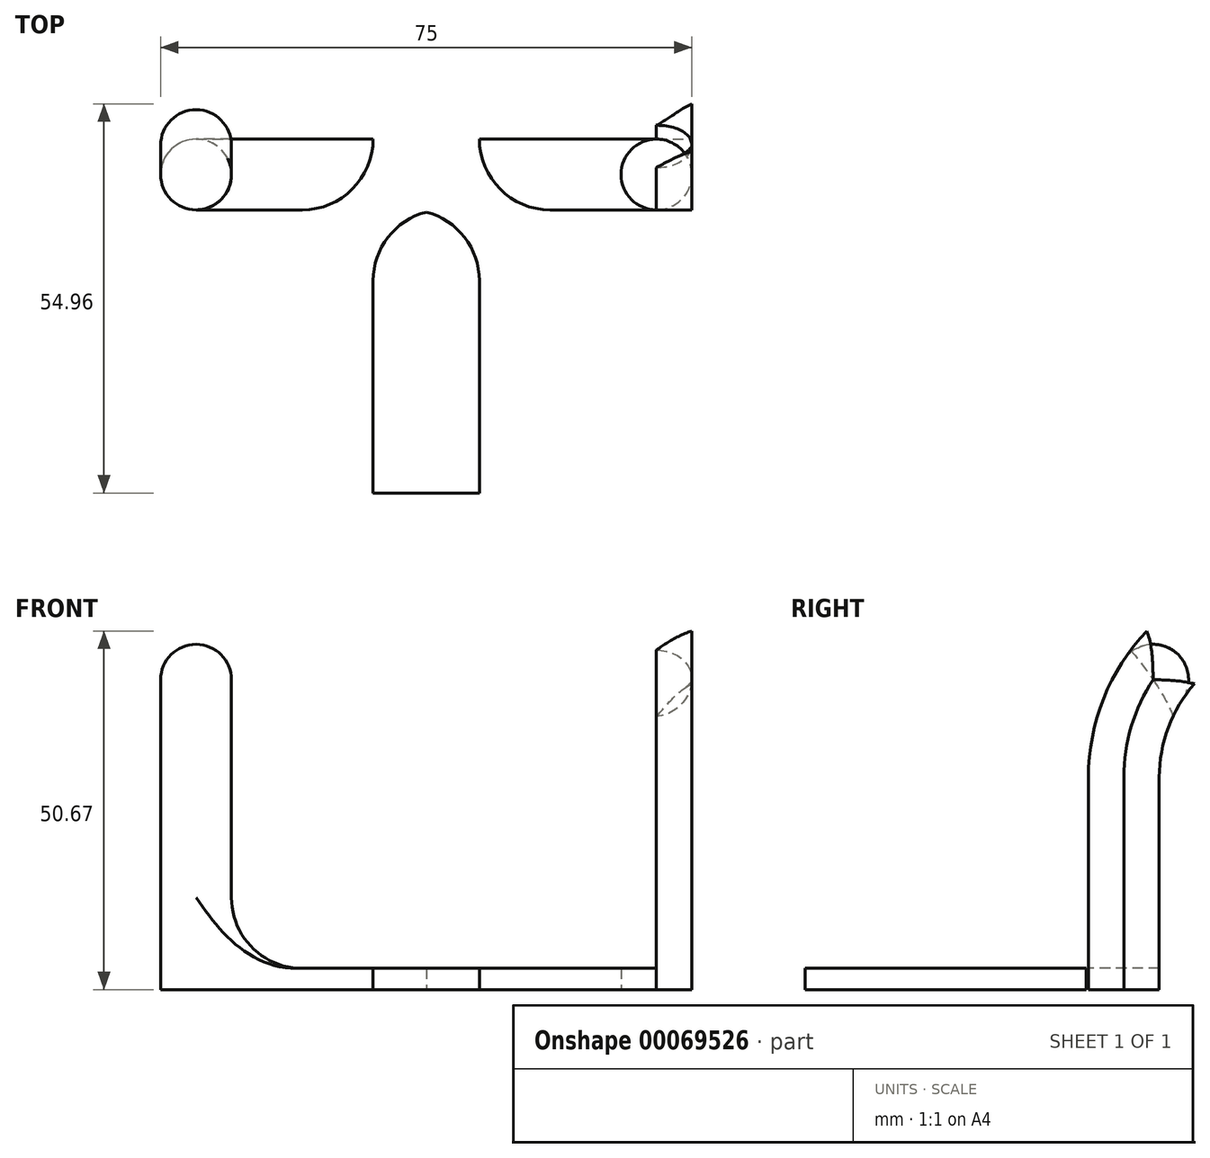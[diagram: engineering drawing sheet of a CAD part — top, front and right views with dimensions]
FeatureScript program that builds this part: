
annotation { "Feature Type Name" : "Feature", "Feature Type Description" : "" }
export const myFeature = defineFeature(function(context is Context, id is Id, definition is map)
    precondition{}
    {
        {
            var Q0;
            Q0=qCreatedBy(makeId("Top.planeOp"),FACE);
            var sketch = newSketch(context, id + "F0", { "sketchPlane" : qUnion([Q0])});
            skLineSegment(sketch, "E0.bottom", {"start": v(-37.5, -5) * mm, "end": v(37.5, -5) * mm});
            skLineSegment(sketch, "E0.top", {"start": v(-37.5, 5) * mm, "end": v(37.5, 5) * mm});
            skLineSegment(sketch, "E0.left", {"start": v(-37.5, -5) * mm, "end": v(-37.5, 5) * mm});
            skLineSegment(sketch, "E0.right", {"start": v(37.5, -5) * mm, "end": v(37.5, 5) * mm});
            skPoint(sketch, "E0.middle", {"position": v(0, 0) * mm});
            skLineSegment(sketch, "E1", {"start": v(0, 0) * mm, "end": v(0, 5) * mm, "construction": true});
            skCircle(sketch, "E2", {"center": v(-32.5, 0) * mm, "radius": 5 * mm});
            skCircle(sketch, "E3.MirrorC", {"center": v(32.5, 0) * mm, "radius": 5 * mm});
            skLineSegment(sketch, "E4.bottom", {"start": v(7.5, -45) * mm, "end": v(-7.5, -45) * mm});
            skLineSegment(sketch, "E4.top", {"start": v(7.5, 5) * mm, "end": v(-7.5, 5) * mm});
            skLineSegment(sketch, "E4.left", {"start": v(7.5, -45) * mm, "end": v(7.5, 5) * mm});
            skLineSegment(sketch, "E4.right", {"start": v(-7.5, -45) * mm, "end": v(-7.5, 5) * mm});
            skPoint(sketch, "E4.middle", {"position": v(0, -20) * mm});
            skSolve(sketch);
        }
        {
            var Q0;
            {var subQ0=sQuery(id+"F0.wireOp",EDGE,"E3.MirrorC");var subQ1=makeQuery(id+"F0.imprint","INTERSECT",VERTEX,{"derivedFrom":[sQuery(id+"F0.wireOp",EDGE,"E0.top"),subQ0]});Q0=makeQuery(id+"F0.imprint","IMPRINT",FACE,{"disambiguationData":[TD([[makeQuery(id+"F0.imprint","IMPRINT",EDGE,{"disambiguationData":[TD([[subQ1,-1.0]])],"derivedFrom":subQ0}),-1.0]])]});}
            var Q1;
            {var subQ0=sQuery(id+"F0.wireOp",EDGE,"E2");var subQ1=makeQuery(id+"F0.imprint","INTERSECT",VERTEX,{"derivedFrom":[sQuery(id+"F0.wireOp",EDGE,"E0.top"),subQ0]});Q1=makeQuery(id+"F0.imprint","IMPRINT",FACE,{"disambiguationData":[TD([[makeQuery(id+"F0.imprint","IMPRINT",EDGE,{"disambiguationData":[TD([[subQ1,-1.0]])],"derivedFrom":subQ0}),1.0]])]});}
            var Q2;
            {var subQ0=sQuery(id+"F0.wireOp",EDGE,"E2");var subQ1=sQuery(id+"F0.wireOp",EDGE,"E0.bottom");var subQ2=makeQuery(id+"F0.imprint","INTERSECT",VERTEX,{"derivedFrom":[subQ1,subQ0]});Q2=makeQuery(id+"F0.imprint","IMPRINT",FACE,{"disambiguationData":[TD([[makeQuery(id+"F0.imprint","IMPRINT",EDGE,{"disambiguationData":[TD([[subQ2,-1.0]])],"derivedFrom":subQ1}),1.0]])]});}
            var Q3;
            {var subQ0=sQuery(id+"F0.wireOp",EDGE,"E4.left");var subQ1=sQuery(id+"F0.wireOp",EDGE,"E0.bottom");var subQ2=makeQuery(id+"F0.imprint","INTERSECT",VERTEX,{"derivedFrom":[subQ1,subQ0]});Q3=makeQuery(id+"F0.imprint","IMPRINT",FACE,{"disambiguationData":[TD([[makeQuery(id+"F0.imprint","IMPRINT",EDGE,{"disambiguationData":[TD([[subQ2,-1.0]])],"derivedFrom":subQ1}),1.0]])]});}
            var Q4;
            {var subQ5=sQuery(id+"F0.wireOp",EDGE,"E4.top");Q4=makeQuery(id+"F0.imprint","IMPRINT",FACE,{"disambiguationData":[TD([[makeQuery(id+"F0.imprint","IMPRINT",EDGE,{"derivedFrom":subQ5}),1.0]])]});}
            var Q5;
            {var subQ5=sQuery(id+"F0.wireOp",EDGE,"E4.bottom");Q5=makeQuery(id+"F0.imprint","IMPRINT",FACE,{"disambiguationData":[TD([[makeQuery(id+"F0.imprint","IMPRINT",EDGE,{"derivedFrom":subQ5}),-1.0]])]});}
            extrude(context, id + "F1", {"entities" : qUnion([Q0, Q1, Q2, Q3, Q4, Q5]), "depth" : 3 * mm});
        }
        {
            var Q0;
            Q0=makeQuery(id+"F0.imprint","IMPRINT",FACE,{"disambiguationData":[TD([[makeQuery(id+"F0.imprint","IMPRINT",EDGE,{"derivedFrom":sQuery(id+"F0.wireOp",EDGE,"E2")}),1.0]])]});
            var Q1;
            Q1=makeQuery(id+"F0.imprint","IMPRINT",FACE,{"disambiguationData":[TD([[makeQuery(id+"F0.imprint","IMPRINT",EDGE,{"derivedFrom":sQuery(id+"F0.wireOp",EDGE,"E3.MirrorC")}),-1.0]])]});
            extrude(context, id + "F2", {"entities" : qUnion([Q0, Q1]), "operationType" : NewBodyOperationType.ADD, "depth" : 30 * mm});
        }
        {
            var Q0;
            Q0=makeQuery(id+"F2.opExtrude","CAP_FACE",FACE,{"disambiguationData":[OSD([sQuery(id+"F0.wireOp",EDGE,"E2")])],"isStart":false});
            var sketch = newSketch(context, id + "F3", { "sketchPlane" : qUnion([Q0])});
            skLineSegment(sketch, "E5", {"start": v(0, 0) * mm, "end": v(0, 25) * mm, "construction": true});
            skLineSegment(sketch, "E6", {"start": v(0, 25) * mm, "end": v(-30, 25) * mm, "construction": true});
            skSolve(sketch);
        }
        {
            var Q0;
            Q0=makeQuery(id+"F3.imprint","IMPRINT",FACE,{"disambiguationData":[TD([[makeQuery(id+"F3.imprint","IMPRINT",EDGE,{"derivedFrom":makeQuery(id+"F2.opExtrude","CAP_EDGE",EDGE,{"disambiguationData":[OSD([sQuery(id+"F0.wireOp",EDGE,"E2")])],"isStart":false})}),1.0]])]});
            var Q1;
            Q1=makeQuery(id+"F2.opExtrude","CAP_FACE",FACE,{"disambiguationData":[OSD([sQuery(id+"F0.wireOp",EDGE,"E3.MirrorC")])],"isStart":false});
            var Q2;
            Q2=sQuery(id+"F3.wireOp",EDGE,"E6");
            revolve(context, id + "F4", {"operationType" : NewBodyOperationType.ADD, "entities" : qUnion([Q0, Q1]), "axis" : qUnion([Q2]), "revolveType" : RevolveType.ONE_DIRECTION, "angle" : 45 * degree});
        }
        {
            var Q0;
            Q0=makeQuery(id+"F4.opRevolve","CAP_EDGE",EDGE,{"disambiguationData":[OSD([sQuery(id+"F0.wireOp",EDGE,"E2")])],"isStart":false});
            var Q1;
            Q1=makeQuery(id+"F4.opRevolve","CAP_EDGE",EDGE,{"disambiguationData":[OSD([sQuery(id+"F0.wireOp",EDGE,"E3.MirrorC")])],"isStart":false});
            fillet(context, id + "F5", {"entities" : qUnion([Q0, Q1]), "radius" : 5 * mm, "tangentPropagation" : true, "allowEdgeOverflow" : false});
        }
        {
            var Q0;
            {var subQ0=sQuery(id+"F0.wireOp",EDGE,"E2");Q0=makeQuery(id+"F2.boolean.opBoolean","INTERSECT",EDGE,{"derivedFrom":[makeQuery(id+"F1.opExtrude","CAP_FACE",FACE,{"disambiguationData":[OSD([sQuery(id+"F0.wireOp",EDGE,"E0.bottom"),sQuery(id+"F0.wireOp",EDGE,"E0.top"),subQ0,sQuery(id+"F0.wireOp",EDGE,"E3.MirrorC"),sQuery(id+"F0.wireOp",EDGE,"E4.bottom"),sQuery(id+"F0.wireOp",EDGE,"E4.top"),sQuery(id+"F0.wireOp",EDGE,"E4.left"),sQuery(id+"F0.wireOp",EDGE,"E4.right")])],"isStart":false}),makeQuery(id+"F2.opExtrude","SWEPT_FACE",FACE,{"disambiguationData":[OSD([subQ0])]})]});}
            var Q1;
            {var subQ0=sQuery(id+"F0.wireOp",EDGE,"E3.MirrorC");Q1=makeQuery(id+"F2.boolean.opBoolean","INTERSECT",EDGE,{"derivedFrom":[makeQuery(id+"F1.opExtrude","CAP_FACE",FACE,{"disambiguationData":[OSD([sQuery(id+"F0.wireOp",EDGE,"E0.bottom"),sQuery(id+"F0.wireOp",EDGE,"E0.top"),sQuery(id+"F0.wireOp",EDGE,"E2"),subQ0,sQuery(id+"F0.wireOp",EDGE,"E4.bottom"),sQuery(id+"F0.wireOp",EDGE,"E4.top"),sQuery(id+"F0.wireOp",EDGE,"E4.left"),sQuery(id+"F0.wireOp",EDGE,"E4.right")])],"isStart":false}),makeQuery(id+"F2.opExtrude","SWEPT_FACE",FACE,{"disambiguationData":[OSD([subQ0])]})]});}
            var Q2;
            Q2=makeQuery(id+"F1.opExtrude","SWEPT_EDGE",EDGE,{"disambiguationData":[OSD([sQuery(id+"F0.wireOp",EDGE,"E0.bottom"),sQuery(id+"F0.wireOp",EDGE,"E4.right")])]});
            var Q3;
            Q3=makeQuery(id+"F1.opExtrude","SWEPT_EDGE",EDGE,{"disambiguationData":[OSD([sQuery(id+"F0.wireOp",EDGE,"E0.bottom"),sQuery(id+"F0.wireOp",EDGE,"E4.left")])]});
            fillet(context, id + "F6", {"entities" : qUnion([Q0, Q1, Q2, Q3]), "radius" : 10 * mm, "tangentPropagation" : true, "allowEdgeOverflow" : false});
        }
    });
